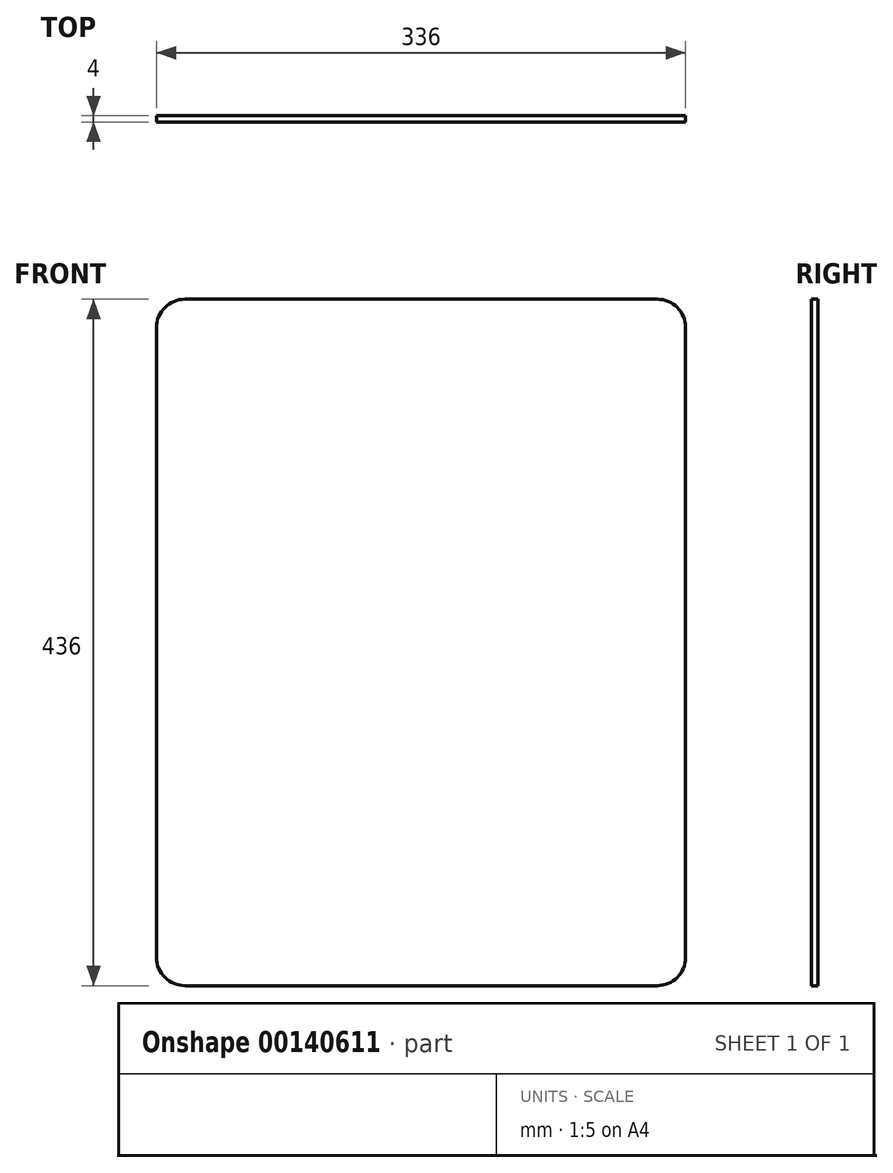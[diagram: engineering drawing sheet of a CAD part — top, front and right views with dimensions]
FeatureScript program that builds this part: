
annotation { "Feature Type Name" : "Feature", "Feature Type Description" : "" }
export const myFeature = defineFeature(function(context is Context, id is Id, definition is map)
    precondition{}
    {
        {
            var Q0;
            Q0=qCreatedBy(makeId("Front.planeOp"),FACE);
            var sketch = newSketch(context, id + "F0", { "sketchPlane" : qUnion([Q0])});
            skLineSegment(sketch, "E0.bottom", {"start": v(-168.67, -249.88) * mm, "end": v(167.33, -249.88) * mm});
            skLineSegment(sketch, "E0.top", {"start": v(-168.67, 186.12) * mm, "end": v(167.33, 186.12) * mm});
            skLineSegment(sketch, "E0.left", {"start": v(-168.67, -249.88) * mm, "end": v(-168.67, 186.12) * mm});
            skLineSegment(sketch, "E0.right", {"start": v(167.33, -249.88) * mm, "end": v(167.33, 186.12) * mm});
            skPoint(sketch, "E0.middle", {"position": v(-0.67, -31.88) * mm});
            skSolve(sketch);
        }
        {
            var Q0;
            Q0 = qSketchRegion(id + "F0", true);
            extrude(context, id + "F1", {"entities" : qUnion([Q0]), "depth" : 4 * mm, "offsetDistance" : 25 * mm});
        }
        {
            var Q0;
            Q0=makeQuery(id+"F1.opExtrude","SWEPT_EDGE",EDGE,{"disambiguationData":[OSD([sQuery(id+"F0.wireOp",EDGE,"E0.top"),sQuery(id+"F0.wireOp",EDGE,"E0.left")])]});
            var Q1;
            Q1=makeQuery(id+"F1.opExtrude","SWEPT_EDGE",EDGE,{"disambiguationData":[OSD([sQuery(id+"F0.wireOp",EDGE,"E0.bottom"),sQuery(id+"F0.wireOp",EDGE,"E0.left")])]});
            var Q2;
            Q2=makeQuery(id+"F1.opExtrude","SWEPT_EDGE",EDGE,{"disambiguationData":[OSD([sQuery(id+"F0.wireOp",EDGE,"E0.top"),sQuery(id+"F0.wireOp",EDGE,"E0.right")])]});
            var Q3;
            Q3=makeQuery(id+"F1.opExtrude","SWEPT_EDGE",EDGE,{"disambiguationData":[OSD([sQuery(id+"F0.wireOp",EDGE,"E0.bottom"),sQuery(id+"F0.wireOp",EDGE,"E0.right")])]});
            fillet(context, id + "F2", {"entities" : qUnion([Q0, Q1, Q2, Q3]), "radius" : 18 * mm, "tangentPropagation" : true, "allowEdgeOverflow" : false});
        }
    });
